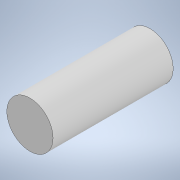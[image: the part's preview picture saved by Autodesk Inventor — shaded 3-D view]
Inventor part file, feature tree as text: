
AUTODESK INVENTOR PART (.ipt)
format: ipt  version: 2021 (Build 250183000, 183)  size: 91,136 bytes
history: native  units: mm
features: extrude x1, sketch x1
ambient origin geometry x8: Origin, YZ Plane, XZ Plane, XY Plane, X Axis, Y Axis, Z Axis, Center Point
bodies: Solid1 (feature_tree)
feature tree (2):
  extrude  "Extrusion1"  Depth=13.0mm TaperAngle=0.0deg
  sketch  "Sketch1"  dims[d0=5.0mm d1=13.0mm d2=0.0mm]
